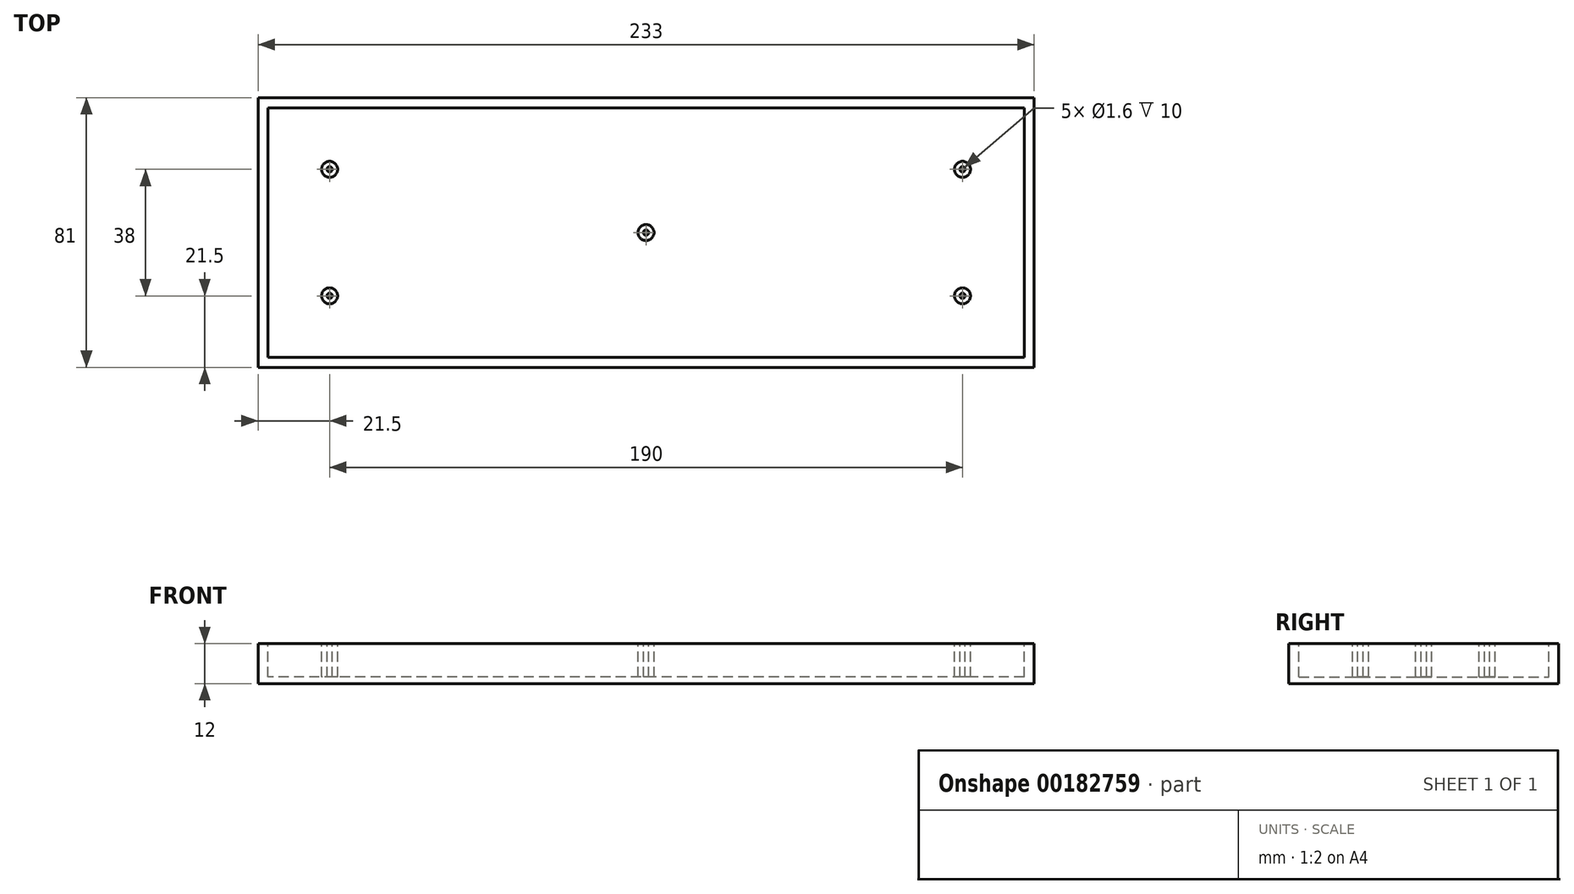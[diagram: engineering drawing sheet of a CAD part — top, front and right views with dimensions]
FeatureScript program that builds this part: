
annotation { "Feature Type Name" : "Feature", "Feature Type Description" : "" }
export const myFeature = defineFeature(function(context is Context, id is Id, definition is map)
    precondition{}
    {
        {
            var Q0;
            Q0=qCreatedBy(makeId("Top.planeOp"),FACE);
            var sketch = newSketch(context, id + "F0", { "sketchPlane" : qUnion([Q0])});
            skLineSegment(sketch, "E0.bottom", {"start": v(116.5, -40.5) * mm, "end": v(-116.5, -40.5) * mm});
            skLineSegment(sketch, "E0.top", {"start": v(116.5, 40.5) * mm, "end": v(-116.5, 40.5) * mm});
            skLineSegment(sketch, "E0.left", {"start": v(116.5, -40.5) * mm, "end": v(116.5, 40.5) * mm});
            skLineSegment(sketch, "E0.right", {"start": v(-116.5, -40.5) * mm, "end": v(-116.5, 40.5) * mm});
            skPoint(sketch, "E0.middle", {"position": v(0, 0) * mm});
            skSolve(sketch);
        }
        {
            var Q0;
            Q0 = qSketchRegion(id + "F0", true);
            extrude(context, id + "F1", {"entities" : qUnion([Q0]), "depth" : 12 * mm});
        }
        {
            var Q0;
            Q0=makeQuery(id+"F1.opExtrude","CAP_FACE",FACE,{"disambiguationData":[OSD([sQuery(id+"F0.wireOp",EDGE,"E0.bottom"),sQuery(id+"F0.wireOp",EDGE,"E0.top"),sQuery(id+"F0.wireOp",EDGE,"E0.left"),sQuery(id+"F0.wireOp",EDGE,"E0.right")])],"isStart":false});
            var sketch = newSketch(context, id + "F2", { "sketchPlane" : qUnion([Q0])});
            skCircle(sketch, "E1", {"center": v(-95, 19) * mm, "radius": 0.8 * mm});
            skCircle(sketch, "E2", {"center": v(-95, -19) * mm, "radius": 0.8 * mm});
            skCircle(sketch, "E3", {"center": v(95, -19) * mm, "radius": 0.8 * mm});
            skCircle(sketch, "E4", {"center": v(95, 19) * mm, "radius": 0.8 * mm});
            skCircle(sketch, "E5", {"center": v(0, 0) * mm, "radius": 0.8 * mm});
            skCircle(sketch, "E6", {"center": v(-95, 19) * mm, "radius": 2.4 * mm});
            skCircle(sketch, "E7", {"center": v(-95, -19) * mm, "radius": 2.4 * mm});
            skCircle(sketch, "E8", {"center": v(95, 19) * mm, "radius": 2.4 * mm});
            skCircle(sketch, "E9", {"center": v(95, -19) * mm, "radius": 2.4 * mm});
            skCircle(sketch, "E10", {"center": v(0, 0) * mm, "radius": 2.4 * mm});
            skLineSegment(sketch, "E11.bottom", {"start": v(113.5, -37.5) * mm, "end": v(-113.5, -37.5) * mm});
            skLineSegment(sketch, "E11.top", {"start": v(113.5, 37.5) * mm, "end": v(-113.5, 37.5) * mm});
            skLineSegment(sketch, "E11.left", {"start": v(113.5, -37.5) * mm, "end": v(113.5, 37.5) * mm});
            skLineSegment(sketch, "E11.right", {"start": v(-113.5, -37.5) * mm, "end": v(-113.5, 37.5) * mm});
            skSolve(sketch);
        }
        {
            var Q0;
            Q0=makeQuery(id+"F2.imprint","IMPRINT",FACE,{"disambiguationData":[TD([[makeQuery(id+"F2.imprint","IMPRINT",EDGE,{"derivedFrom":sQuery(id+"F2.wireOp",EDGE,"E1")}),1.0]])]});
            var Q1;
            Q1=makeQuery(id+"F2.imprint","IMPRINT",FACE,{"disambiguationData":[TD([[makeQuery(id+"F2.imprint","IMPRINT",EDGE,{"derivedFrom":sQuery(id+"F2.wireOp",EDGE,"E6")}),-1.0]])]});
            var Q2;
            Q2=makeQuery(id+"F2.imprint","IMPRINT",FACE,{"disambiguationData":[TD([[makeQuery(id+"F2.imprint","IMPRINT",EDGE,{"derivedFrom":sQuery(id+"F2.wireOp",EDGE,"E2")}),1.0]])]});
            var Q3;
            Q3=makeQuery(id+"F2.imprint","IMPRINT",FACE,{"disambiguationData":[TD([[makeQuery(id+"F2.imprint","IMPRINT",EDGE,{"derivedFrom":sQuery(id+"F2.wireOp",EDGE,"E5")}),1.0]])]});
            var Q4;
            Q4=makeQuery(id+"F2.imprint","IMPRINT",FACE,{"disambiguationData":[TD([[makeQuery(id+"F2.imprint","IMPRINT",EDGE,{"derivedFrom":sQuery(id+"F2.wireOp",EDGE,"E4")}),1.0]])]});
            var Q5;
            Q5=makeQuery(id+"F2.imprint","IMPRINT",FACE,{"disambiguationData":[TD([[makeQuery(id+"F2.imprint","IMPRINT",EDGE,{"derivedFrom":sQuery(id+"F2.wireOp",EDGE,"E3")}),1.0]])]});
            extrude(context, id + "F3", {"entities" : qUnion([Q0, Q1, Q2, Q3, Q4, Q5]), "operationType" : NewBodyOperationType.REMOVE, "oppositeDirection" : true, "depth" : 10 * mm});
        }
    });
